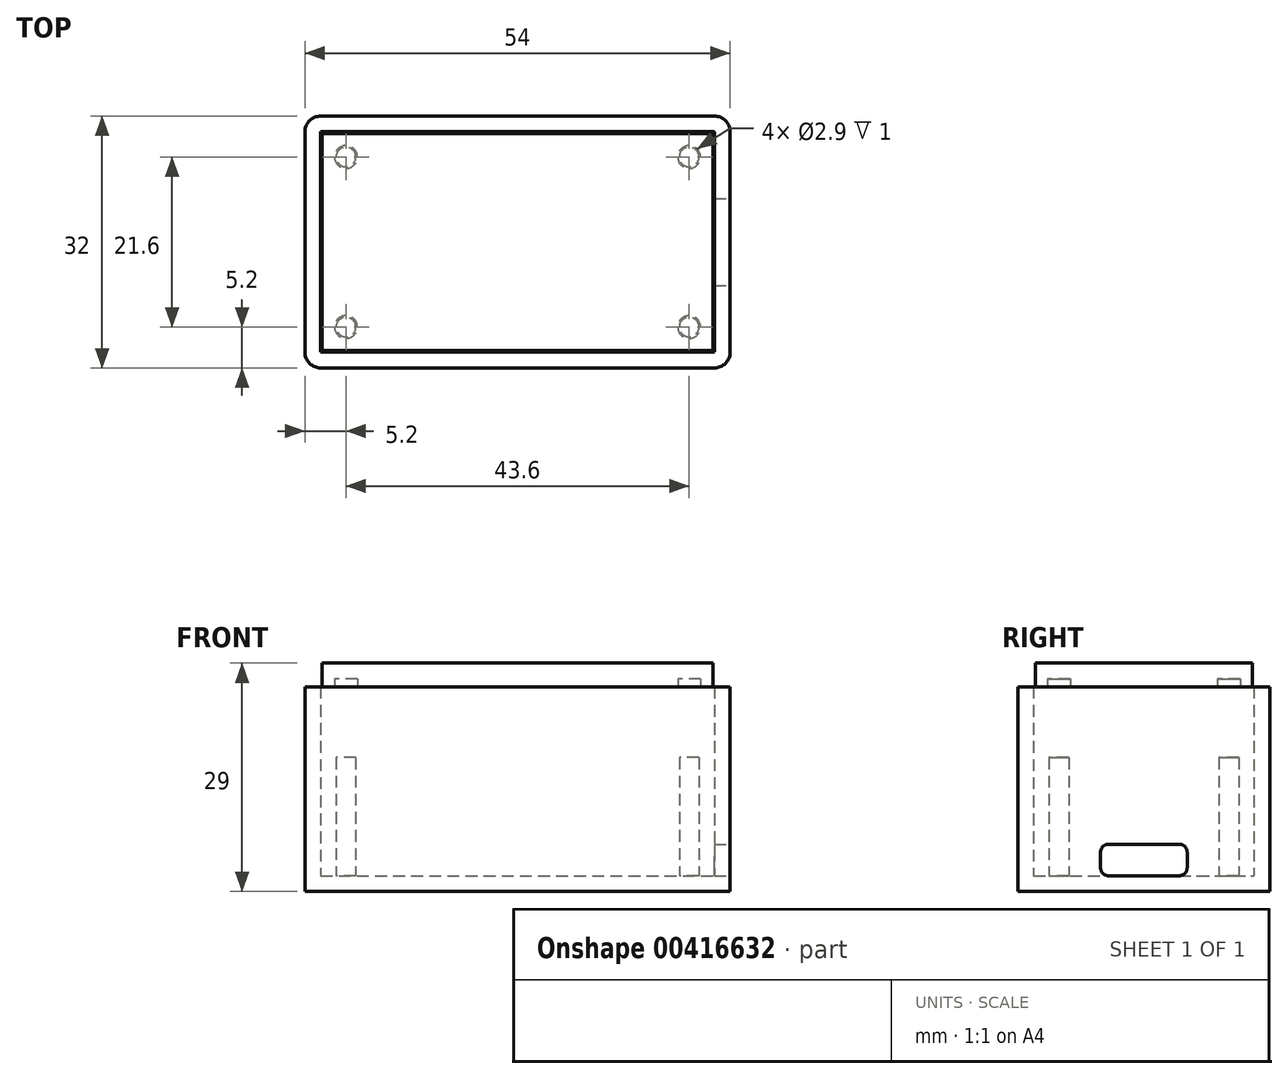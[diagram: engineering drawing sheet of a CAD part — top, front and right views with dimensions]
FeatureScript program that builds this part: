
annotation { "Feature Type Name" : "Feature", "Feature Type Description" : "" }
export const myFeature = defineFeature(function(context is Context, id is Id, definition is map)
    precondition{}
    {
        {
            var Q0;
            Q0=qCreatedBy(makeId("Top.planeOp"),FACE);
            var sketch = newSketch(context, id + "F0", { "sketchPlane" : qUnion([Q0])});
            skLineSegment(sketch, "E0.bottom", {"start": v(-22.94, -13) * mm, "end": v(25.06, -13) * mm});
            skLineSegment(sketch, "E0.top", {"start": v(-22.94, 13) * mm, "end": v(25.06, 13) * mm});
            skLineSegment(sketch, "E0.left", {"start": v(-22.94, -13) * mm, "end": v(-22.94, 13) * mm});
            skLineSegment(sketch, "E0.right", {"start": v(25.06, -13) * mm, "end": v(25.06, 13) * mm});
            skPoint(sketch, "E0.middle", {"position": v(1.06, 0) * mm});
            skCircle(sketch, "E1", {"center": v(-20.74, 10.8) * mm, "radius": 1.5 * mm});
            skCircle(sketch, "E2", {"center": v(22.86, 10.8) * mm, "radius": 1.5 * mm});
            skCircle(sketch, "E3", {"center": v(-20.74, -10.8) * mm, "radius": 1.5 * mm});
            skCircle(sketch, "E4", {"center": v(22.86, -10.8) * mm, "radius": 1.5 * mm});
            skLineSegment(sketch, "E5.bottom", {"start": v(26.56, 4.1) * mm, "end": v(21.06, 4.1) * mm});
            skLineSegment(sketch, "E5.top", {"start": v(26.56, -4.1) * mm, "end": v(21.06, -4.1) * mm});
            skLineSegment(sketch, "E5.left", {"start": v(26.56, 4.1) * mm, "end": v(26.56, -4.1) * mm});
            skLineSegment(sketch, "E5.right", {"start": v(21.06, 4.1) * mm, "end": v(21.06, -4.1) * mm});
            skPoint(sketch, "E5.middle", {"position": v(23.81, 0) * mm});
            skPoint(sketch, "E5.middle.positionSnap0", {"position": v(25.06, 0) * mm});
            skPoint(sketch, "E5.centerSnap0", {"position": v(25.06, 0) * mm});
            skLineSegment(sketch, "E6.bottom", {"start": v(-22.94, 8) * mm, "end": v(2.06, 8) * mm});
            skLineSegment(sketch, "E6.top", {"start": v(-22.94, -8) * mm, "end": v(2.06, -8) * mm});
            skLineSegment(sketch, "E6.left", {"start": v(-22.94, 8) * mm, "end": v(-22.94, -8) * mm});
            skLineSegment(sketch, "E6.right", {"start": v(2.06, 8) * mm, "end": v(2.06, -8) * mm});
            skPoint(sketch, "E6.middle", {"position": v(-10.44, 0) * mm});
            skLineSegment(sketch, "E7.bottom", {"start": v(-22.94, 13) * mm, "end": v(15.06, 13) * mm});
            skLineSegment(sketch, "E7.left", {"start": v(-22.94, 13) * mm, "end": v(-22.94, 10.3) * mm});
            skLineSegment(sketch, "E8.bottom", {"start": v(-22.94, -13) * mm, "end": v(15.06, -13) * mm});
            skLineSegment(sketch, "E8.left", {"start": v(-22.94, -13) * mm, "end": v(-22.94, -10.3) * mm});
            skSolve(sketch);
        }
        {
            var Q0;
            Q0=qCreatedBy(makeId("Top.planeOp"),FACE);
            var sketch = newSketch(context, id + "F1", { "sketchPlane" : qUnion([Q0])});
            skLineSegment(sketch, "E9.bottom", {"start": v(-23.94, -14) * mm, "end": v(26.06, -14) * mm});
            skLineSegment(sketch, "E9.top", {"start": v(-23.94, 14) * mm, "end": v(26.06, 14) * mm});
            skLineSegment(sketch, "E9.left", {"start": v(-23.94, -14) * mm, "end": v(-23.94, 14) * mm});
            skLineSegment(sketch, "E9.right", {"start": v(26.06, -14) * mm, "end": v(26.06, 14) * mm});
            skCircle(sketch, "E10", {"center": v(-20.74, -10.8) * mm, "radius": 1.25 * mm});
            skCircle(sketch, "E11", {"center": v(-20.74, 10.8) * mm, "radius": 1.25 * mm});
            skCircle(sketch, "E12", {"center": v(22.86, 10.8) * mm, "radius": 1.25 * mm});
            skCircle(sketch, "E13", {"center": v(22.86, -10.8) * mm, "radius": 1.25 * mm});
            skSolve(sketch);
        }
        {
            var Q0;
            Q0=makeQuery(id+"F1.imprint","IMPRINT",FACE,{"disambiguationData":[TD([[makeQuery(id+"F1.imprint","IMPRINT",EDGE,{"derivedFrom":sQuery(id+"F1.wireOp",EDGE,"E13")}),1.0]])]});
            var Q1;
            Q1=makeQuery(id+"F1.imprint","IMPRINT",FACE,{"disambiguationData":[TD([[makeQuery(id+"F1.imprint","IMPRINT",EDGE,{"derivedFrom":sQuery(id+"F1.wireOp",EDGE,"E10")}),1.0]])]});
            var Q2;
            Q2=makeQuery(id+"F1.imprint","IMPRINT",FACE,{"disambiguationData":[TD([[makeQuery(id+"F1.imprint","IMPRINT",EDGE,{"derivedFrom":sQuery(id+"F1.wireOp",EDGE,"E11")}),1.0]])]});
            var Q3;
            Q3=makeQuery(id+"F1.imprint","IMPRINT",FACE,{"disambiguationData":[TD([[makeQuery(id+"F1.imprint","IMPRINT",EDGE,{"derivedFrom":sQuery(id+"F1.wireOp",EDGE,"E12")}),1.0]])]});
            var Q4;
            Q4=makeQuery(id+"F1.imprint","IMPRINT",FACE,{"disambiguationData":[TD([[makeQuery(id+"F1.imprint","IMPRINT",EDGE,{"derivedFrom":sQuery(id+"F1.wireOp",EDGE,"E9.bottom")}),1.0]])]});
            extrude(context, id + "F2", {"entities" : qUnion([Q0, Q1, Q2, Q3, Q4]), "depth" : 24 * mm});
        }
        {
            var Q0;
            Q0=makeQuery(id+"F2.opExtrude","CAP_FACE",FACE,{"disambiguationData":[OSD([sQuery(id+"F1.wireOp",EDGE,"E9.bottom"),sQuery(id+"F1.wireOp",EDGE,"E9.top"),sQuery(id+"F1.wireOp",EDGE,"E9.left"),sQuery(id+"F1.wireOp",EDGE,"E9.right")])],"isStart":false});
            shell(context, id + "F3", {"entities" : qUnion([Q0]), "thickness" : 2 * mm, "oppositeDirection" : true});
        }
        {
            var Q0;
            Q0=makeQuery(id+"F1.imprint","IMPRINT",FACE,{"disambiguationData":[TD([[makeQuery(id+"F1.imprint","IMPRINT",EDGE,{"derivedFrom":sQuery(id+"F1.wireOp",EDGE,"E10")}),1.0]])]});
            var Q1;
            Q1=makeQuery(id+"F1.imprint","IMPRINT",FACE,{"disambiguationData":[TD([[makeQuery(id+"F1.imprint","IMPRINT",EDGE,{"derivedFrom":sQuery(id+"F1.wireOp",EDGE,"E11")}),1.0]])]});
            var Q2;
            Q2=makeQuery(id+"F1.imprint","IMPRINT",FACE,{"disambiguationData":[TD([[makeQuery(id+"F1.imprint","IMPRINT",EDGE,{"derivedFrom":sQuery(id+"F1.wireOp",EDGE,"E13")}),1.0]])]});
            var Q3;
            Q3=makeQuery(id+"F1.imprint","IMPRINT",FACE,{"disambiguationData":[TD([[makeQuery(id+"F1.imprint","IMPRINT",EDGE,{"derivedFrom":sQuery(id+"F1.wireOp",EDGE,"E12")}),1.0]])]});
            var Q4;
            Q4=sQuery(id+"F1.wireOp",EDGE,"E11");
            var Q5;
            Q5=sQuery(id+"F1.wireOp",EDGE,"E10");
            var Q6;
            Q6=sQuery(id+"F1.wireOp",EDGE,"E13");
            var Q7;
            Q7=sQuery(id+"F1.wireOp",EDGE,"E12");
            extrude(context, id + "F4", {"entities" : qUnion([Q0, Q1, Q2, Q3]), "operationType" : NewBodyOperationType.ADD, "surfaceEntities" : qUnion([Q4, Q5, Q6, Q7]), "depth" : 15 * mm});
        }
        {
            var Q0;
            Q0=makeQuery(id+"F2.opExtrude","SWEPT_EDGE",EDGE,{"disambiguationData":[OSD([sQuery(id+"F1.wireOp",EDGE,"E9.top"),sQuery(id+"F1.wireOp",EDGE,"E9.left")])]});
            var Q1;
            Q1=makeQuery(id+"F2.opExtrude","SWEPT_EDGE",EDGE,{"disambiguationData":[OSD([sQuery(id+"F1.wireOp",EDGE,"E9.bottom"),sQuery(id+"F1.wireOp",EDGE,"E9.left")])]});
            var Q2;
            Q2=makeQuery(id+"F2.opExtrude","SWEPT_EDGE",EDGE,{"disambiguationData":[OSD([sQuery(id+"F1.wireOp",EDGE,"E9.bottom"),sQuery(id+"F1.wireOp",EDGE,"E9.right")])]});
            var Q3;
            Q3=makeQuery(id+"F2.opExtrude","SWEPT_EDGE",EDGE,{"disambiguationData":[OSD([sQuery(id+"F1.wireOp",EDGE,"E9.top"),sQuery(id+"F1.wireOp",EDGE,"E9.right")])]});
            fillet(context, id + "F5", {"entities" : qUnion([Q0, Q1, Q2, Q3]), "radius" : 2 * mm, "tangentPropagation" : true, "allowEdgeOverflow" : false});
        }
        {
            var Q0;
            Q0=makeQuery(id+"F2.opExtrude","SWEPT_FACE",FACE,{"disambiguationData":[OSD([sQuery(id+"F1.wireOp",EDGE,"E9.right")])]});
            var sketch = newSketch(context, id + "F6", { "sketchPlane" : qUnion([Q0])});
            skLineSegment(sketch, "E14.bottom", {"start": v(5.5, 0) * mm, "end": v(-5.5, 0) * mm});
            skLineSegment(sketch, "E14.top", {"start": v(5.5, 4) * mm, "end": v(-5.5, 4) * mm});
            skLineSegment(sketch, "E14.left", {"start": v(5.5, 0) * mm, "end": v(5.5, 4) * mm});
            skLineSegment(sketch, "E14.right", {"start": v(-5.5, 0) * mm, "end": v(-5.5, 4) * mm});
            skSolve(sketch);
        }
        {
            var Q0;
            Q0=qSketchRegion(id+"F6",true);
            extrude(context, id + "F7", {"entities" : qUnion([Q0]), "operationType" : NewBodyOperationType.REMOVE, "oppositeDirection" : true, "depth" : 2 * mm});
        }
        {
            var Q0;
            Q0=makeQuery(id+"F7.boolean.opBoolean","COPY",EDGE,{"derivedFrom":makeQuery(id+"F7.opExtrude","SWEPT_EDGE",EDGE,{"disambiguationData":[OSD([sQuery(id+"F6.wireOp",EDGE,"E14.top"),sQuery(id+"F6.wireOp",EDGE,"E14.left")])]})});
            var Q1;
            Q1=makeQuery(id+"F7.boolean.opBoolean","COPY",EDGE,{"derivedFrom":makeQuery(id+"F7.opExtrude","SWEPT_EDGE",EDGE,{"disambiguationData":[OSD([sQuery(id+"F6.wireOp",EDGE,"E14.top"),sQuery(id+"F6.wireOp",EDGE,"E14.right")])]})});
            var Q2;
            Q2=makeQuery(id+"F7.boolean.opBoolean","COPY",EDGE,{"derivedFrom":makeQuery(id+"F7.opExtrude","SWEPT_EDGE",EDGE,{"disambiguationData":[OSD([sQuery(id+"F6.wireOp",EDGE,"E14.bottom"),sQuery(id+"F6.wireOp",EDGE,"E14.left")])]})});
            var Q3;
            Q3=makeQuery(id+"F7.boolean.opBoolean","COPY",EDGE,{"derivedFrom":makeQuery(id+"F7.opExtrude","SWEPT_EDGE",EDGE,{"disambiguationData":[OSD([sQuery(id+"F6.wireOp",EDGE,"E14.bottom"),sQuery(id+"F6.wireOp",EDGE,"E14.right")])]})});
            fillet(context, id + "F8", {"entities" : qUnion([Q0, Q1, Q2, Q3]), "radius" : 1 * mm, "tangentPropagation" : true, "allowEdgeOverflow" : false});
        }
        {
            var Q0;
            Q0=makeQuery(id+"F2.opExtrude","CAP_FACE",FACE,{"disambiguationData":[OSD([sQuery(id+"F1.wireOp",EDGE,"E9.bottom"),sQuery(id+"F1.wireOp",EDGE,"E9.top"),sQuery(id+"F1.wireOp",EDGE,"E9.left"),sQuery(id+"F1.wireOp",EDGE,"E9.right")])],"isStart":false});
            var sketch = newSketch(context, id + "F9", { "sketchPlane" : qUnion([Q0])});
            skCircle(sketch, "E15.0", {"center": v(-20.74, -10.8) * mm, "radius": 1.45 * mm});
            skCircle(sketch, "E16.0", {"center": v(-20.74, 10.8) * mm, "radius": 1.45 * mm});
            skCircle(sketch, "E17.0", {"center": v(22.86, -10.8) * mm, "radius": 1.45 * mm});
            skCircle(sketch, "E18.0", {"center": v(22.86, 10.8) * mm, "radius": 1.45 * mm});
            skLineSegment(sketch, "E19.0", {"start": v(25.86, 13.8) * mm, "end": v(-23.74, 13.8) * mm});
            skLineSegment(sketch, "E19.1", {"start": v(25.86, -13.8) * mm, "end": v(25.86, 13.8) * mm});
            skLineSegment(sketch, "E19.2", {"start": v(-23.74, -13.8) * mm, "end": v(25.86, -13.8) * mm});
            skLineSegment(sketch, "E19.3", {"start": v(-23.74, 13.8) * mm, "end": v(-23.74, -13.8) * mm});
            skSolve(sketch);
        }
        {
            var Q0;
            Q0=makeQuery(id+"F9.imprint","IMPRINT",FACE,{"disambiguationData":[TD([[makeQuery(id+"F9.imprint","IMPRINT",EDGE,{"derivedFrom":sQuery(id+"F9.wireOp",EDGE,"E15.0")}),-1.0]])]});
            var Q1;
            Q1=makeQuery(id+"F9.imprint","IMPRINT",FACE,{"disambiguationData":[TD([[makeQuery(id+"F9.imprint","IMPRINT",EDGE,{"derivedFrom":sQuery(id+"F9.wireOp",EDGE,"E15.0")}),1.0]])]});
            var Q2;
            Q2=makeQuery(id+"F9.imprint","IMPRINT",FACE,{"disambiguationData":[TD([[makeQuery(id+"F9.imprint","IMPRINT",EDGE,{"derivedFrom":sQuery(id+"F9.wireOp",EDGE,"E17.0")}),1.0]])]});
            var Q3;
            Q3=makeQuery(id+"F9.imprint","IMPRINT",FACE,{"disambiguationData":[TD([[makeQuery(id+"F9.imprint","IMPRINT",EDGE,{"derivedFrom":sQuery(id+"F9.wireOp",EDGE,"E18.0")}),1.0]])]});
            var Q4;
            Q4=makeQuery(id+"F9.imprint","IMPRINT",FACE,{"disambiguationData":[TD([[makeQuery(id+"F9.imprint","IMPRINT",EDGE,{"derivedFrom":sQuery(id+"F9.wireOp",EDGE,"E16.0")}),1.0]])]});
            var Q5;
            Q5=sQuery(id+"F9.wireOp",EDGE,"E19.2");
            var Q6;
            Q6=sQuery(id+"F9.wireOp",EDGE,"E19.3");
            var Q7;
            Q7=sQuery(id+"F9.wireOp",EDGE,"E19.0");
            var Q8;
            Q8=sQuery(id+"F9.wireOp",EDGE,"E19.1");
            extrude(context, id + "F10", {"entities" : qUnion([Q0, Q1, Q2, Q3, Q4]), "surfaceEntities" : qUnion([Q5, Q6, Q7, Q8]), "depth" : 3 * mm});
        }
        {
            var Q0;
            Q0=makeQuery(id+"F9.imprint","IMPRINT",FACE,{"disambiguationData":[TD([[makeQuery(id+"F9.imprint","IMPRINT",EDGE,{"derivedFrom":sQuery(id+"F9.wireOp",EDGE,"E15.0")}),1.0]])]});
            var Q1;
            Q1=makeQuery(id+"F9.imprint","IMPRINT",FACE,{"disambiguationData":[TD([[makeQuery(id+"F9.imprint","IMPRINT",EDGE,{"derivedFrom":sQuery(id+"F9.wireOp",EDGE,"E16.0")}),1.0]])]});
            var Q2;
            Q2=makeQuery(id+"F9.imprint","IMPRINT",FACE,{"disambiguationData":[TD([[makeQuery(id+"F9.imprint","IMPRINT",EDGE,{"derivedFrom":sQuery(id+"F9.wireOp",EDGE,"E18.0")}),1.0]])]});
            var Q3;
            Q3=makeQuery(id+"F9.imprint","IMPRINT",FACE,{"disambiguationData":[TD([[makeQuery(id+"F9.imprint","IMPRINT",EDGE,{"derivedFrom":sQuery(id+"F9.wireOp",EDGE,"E17.0")}),1.0]])]});
            var Q4;
            Q4=sQuery(id+"F9.wireOp",EDGE,"E15.0");
            var Q5;
            Q5=sQuery(id+"F9.wireOp",EDGE,"E17.0");
            var Q6;
            Q6=sQuery(id+"F9.wireOp",EDGE,"E18.0");
            var Q7;
            Q7=sQuery(id+"F9.wireOp",EDGE,"E16.0");
            extrude(context, id + "F11", {"entities" : qUnion([Q0, Q1, Q2, Q3]), "operationType" : NewBodyOperationType.REMOVE, "surfaceEntities" : qUnion([Q4, Q5, Q6, Q7]), "depth" : 1 * mm});
        }
    });
